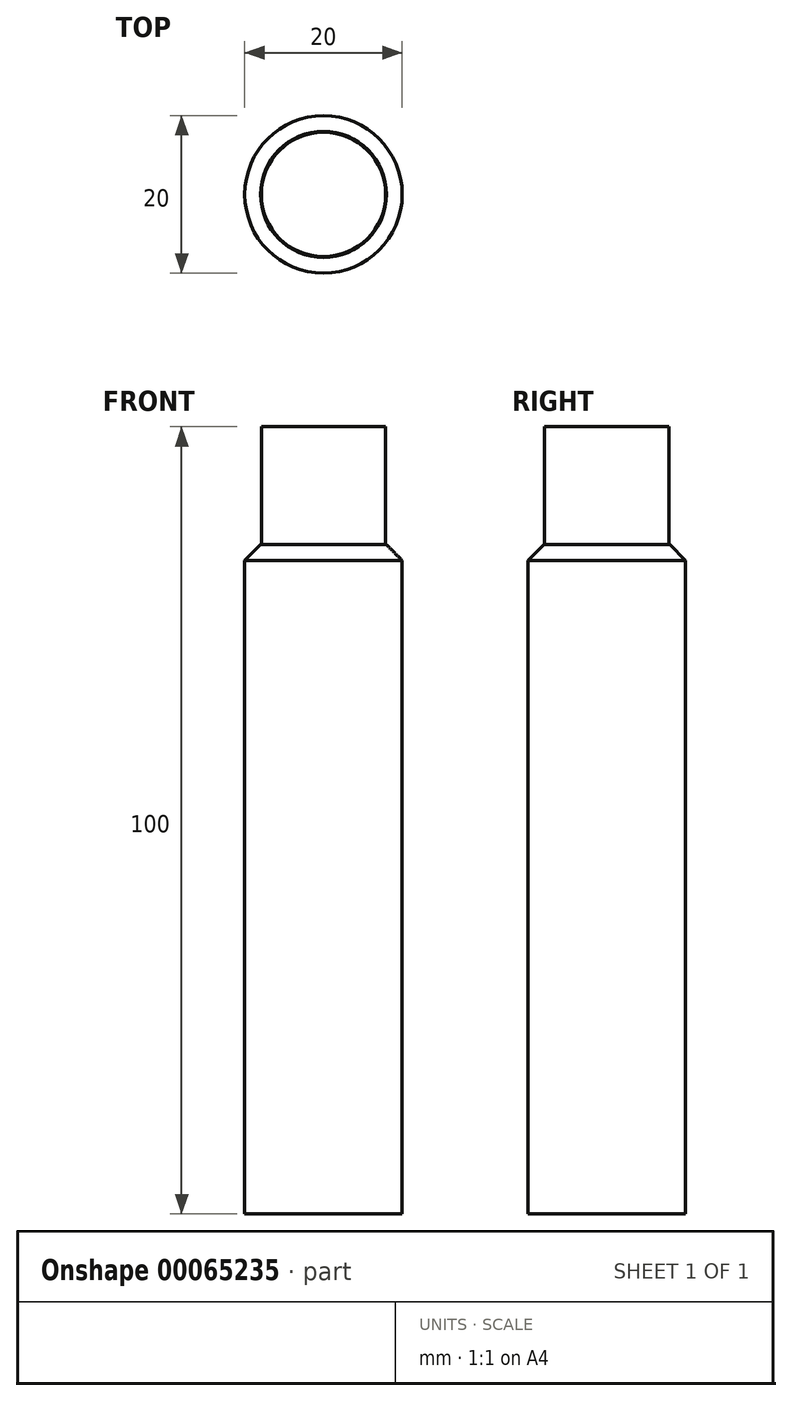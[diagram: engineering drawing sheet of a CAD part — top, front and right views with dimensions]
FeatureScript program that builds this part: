
annotation { "Feature Type Name" : "Feature", "Feature Type Description" : "" }
export const myFeature = defineFeature(function(context is Context, id is Id, definition is map)
    precondition{}
    {
        {
            var Q0;
            Q0=qCreatedBy(makeId("Top.planeOp"),FACE);
            var sketch = newSketch(context, id + "F0", { "sketchPlane" : qUnion([Q0])});
            skCircle(sketch, "E0", {"center": v(0, 0) * mm, "radius": 7.9 * mm});
            skCircle(sketch, "E1", {"center": v(0, 0) * mm, "radius": 10 * mm});
            skSolve(sketch);
        }
        {
            var Q0;
            Q0=makeQuery(id+"F0.imprint","IMPRINT",FACE,{"disambiguationData":[TD([[makeQuery(id+"F0.imprint","IMPRINT",EDGE,{"derivedFrom":sQuery(id+"F0.wireOp",EDGE,"E0")}),1.0]])]});
            extrude(context, id + "F1", {"entities" : qUnion([Q0]), "depth" : 100 * mm});
        }
        {
            var Q0;
            Q0=makeQuery(id+"F0.imprint","IMPRINT",FACE,{"disambiguationData":[TD([[makeQuery(id+"F0.imprint","IMPRINT",EDGE,{"derivedFrom":sQuery(id+"F0.wireOp",EDGE,"E0")}),-1.0]])]});
            extrude(context, id + "F2", {"entities" : qUnion([Q0]), "operationType" : NewBodyOperationType.ADD, "depth" : 85 * mm});
        }
        {
            var Q0;
            Q0=makeQuery(id+"F2.opExtrude","CAP_EDGE",EDGE,{"disambiguationData":[OSD([sQuery(id+"F0.wireOp",EDGE,"E1")])],"isStart":false});
            chamfer(context, id + "F3", {"entities" : qUnion([Q0]), "width" : 2 * mm, "tangentPropagation" : true});
        }
    });
